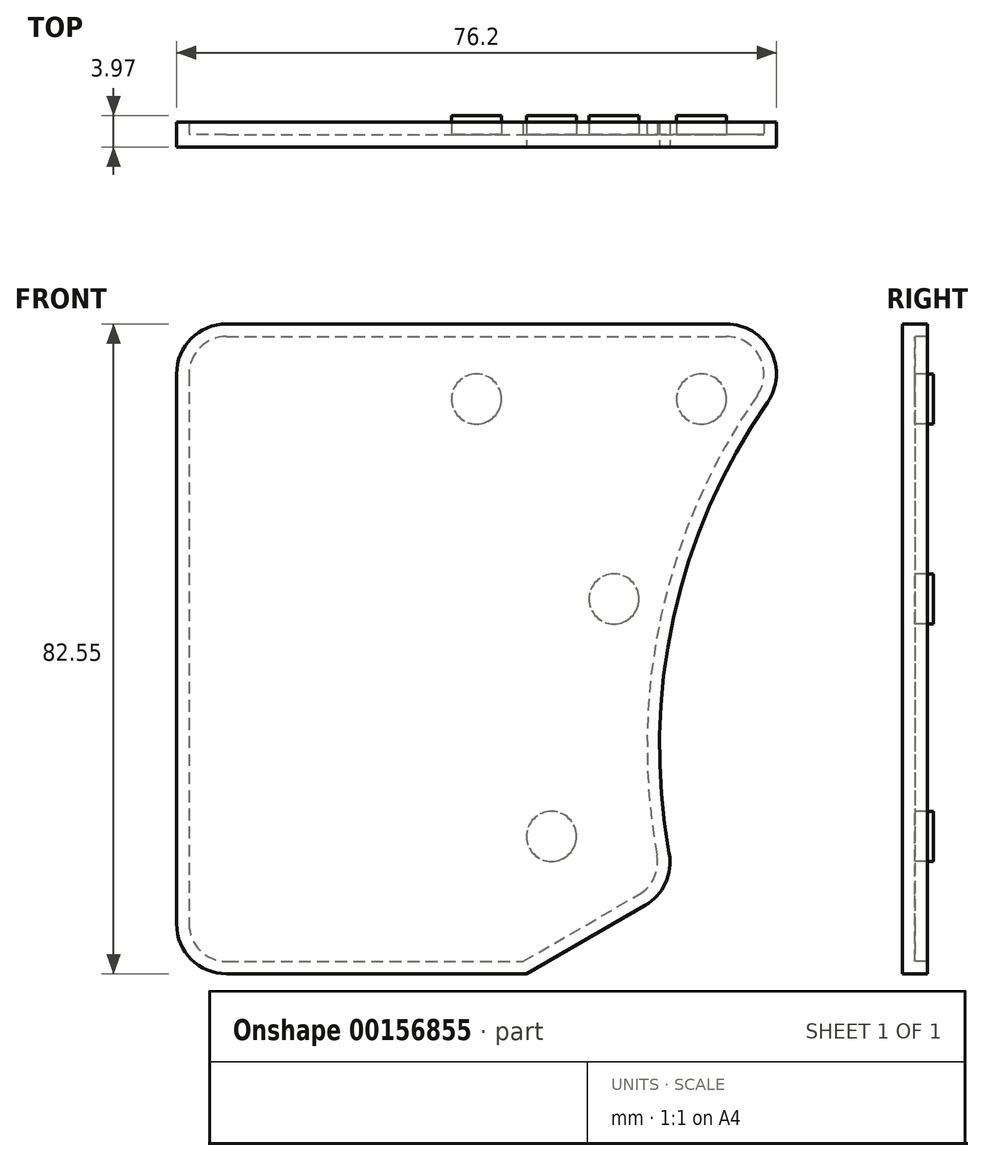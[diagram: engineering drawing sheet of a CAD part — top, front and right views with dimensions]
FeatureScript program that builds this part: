
annotation { "Feature Type Name" : "Feature", "Feature Type Description" : "" }
export const myFeature = defineFeature(function(context is Context, id is Id, definition is map)
    precondition{}
    {
        {
            var Q0;
            Q0=qCreatedBy(makeId("Front.planeOp"),FACE);
            var sketch = newSketch(context, id + "F0", { "sketchPlane" : qUnion([Q0])});
            skLineSegment(sketch, "E0", {"start": v(-19.05, 0) * mm, "end": v(44.45, 0) * mm});
            skLineSegment(sketch, "E1", {"start": v(-25.4, -6.35) * mm, "end": v(-25.4, -76.2) * mm});
            skLineSegment(sketch, "E2", {"start": v(-19.05, -82.55) * mm, "end": v(19.05, -82.55) * mm});
            skArc(sketch, "E3", {"start": v(49.66, -9.98) * mm, "mid": v(50.08, -3.41) * mm, "end": v(44.45, 0) * mm});
            skLineSegment(sketch, "E4", {"start": v(19.05, -82.55) * mm, "end": v(34.1, -73.86) * mm});
            skLineSegment(sketch, "E5", {"start": v(38.1, -71.55) * mm, "end": v(38.1, -82.55) * mm, "construction": true});
            skLineSegment(sketch, "E6", {"start": v(38.1, -82.55) * mm, "end": v(19.05, -82.55) * mm, "construction": true});
            skArc(sketch, "E7", {"start": v(49.66, -9.98) * mm, "mid": v(37.7, -37.35) * mm, "end": v(37.18, -67.22) * mm});
            skPoint(sketch, "E8.visualSharp", {"position": v(38.1, -71.55) * mm});
            skArc(sketch, "E8.filletArc", {"start": v(34.1, -73.86) * mm, "mid": v(36.7, -71.02) * mm, "end": v(37.18, -67.22) * mm});
            skPoint(sketch, "E9", {"position": v(50.8, -6.35) * mm});
            skPoint(sketch, "E10.visualSharp", {"position": v(-25.4, 0) * mm});
            skArc(sketch, "E10.filletArc", {"start": v(-19.05, 0) * mm, "mid": v(-23.54, -1.86) * mm, "end": v(-25.4, -6.35) * mm});
            skPoint(sketch, "E11.visualSharp", {"position": v(-25.4, -82.55) * mm});
            skArc(sketch, "E11.filletArc", {"start": v(-25.4, -76.2) * mm, "mid": v(-23.54, -80.7) * mm, "end": v(-19.05, -82.55) * mm});
            skSolve(sketch);
        }
        {
            var Q0;
            Q0=makeQuery(id+"F0.imprint","IMPRINT",FACE,{"disambiguationData":[TD([[makeQuery(id+"F0.imprint","IMPRINT",EDGE,{"derivedFrom":sQuery(id+"F0.wireOp",EDGE,"E0")}),-1.0]])]});
            extrude(context, id + "F1", {"entities" : qUnion([Q0]), "oppositeDirection" : true, "depth" : 3.17 * mm});
        }
        {
            var Q0;
            Q0=makeQuery(id+"F1.opExtrude","CAP_FACE",FACE,{"disambiguationData":[OSD([sQuery(id+"F0.wireOp",EDGE,"E0"),sQuery(id+"F0.wireOp",EDGE,"E1"),sQuery(id+"F0.wireOp",EDGE,"E2"),sQuery(id+"F0.wireOp",EDGE,"E3"),sQuery(id+"F0.wireOp",EDGE,"E4"),sQuery(id+"F0.wireOp",EDGE,"E7"),sQuery(id+"F0.wireOp",EDGE,"E8.filletArc"),sQuery(id+"F0.wireOp",EDGE,"E10.filletArc"),sQuery(id+"F0.wireOp",EDGE,"E11.filletArc")])],"isStart":false});
            shell(context, id + "F2", {"entities" : qUnion([Q0]), "thickness" : 1.59 * mm});
        }
        {
            var Q0;
            Q0=makeQuery(id+"F2.opShell","OFFSET_FACE",FACE,{"disambiguationData":[OSD([sQuery(id+"F0.wireOp",EDGE,"E0"),sQuery(id+"F0.wireOp",EDGE,"E1"),sQuery(id+"F0.wireOp",EDGE,"E2"),sQuery(id+"F0.wireOp",EDGE,"E3"),sQuery(id+"F0.wireOp",EDGE,"E4"),sQuery(id+"F0.wireOp",EDGE,"E7"),sQuery(id+"F0.wireOp",EDGE,"E8.filletArc"),sQuery(id+"F0.wireOp",EDGE,"E10.filletArc"),sQuery(id+"F0.wireOp",EDGE,"E11.filletArc")])]});
            var sketch = newSketch(context, id + "F3", { "sketchPlane" : qUnion([Q0])});
            skCircle(sketch, "E12", {"center": v(-41.28, -9.53) * mm, "radius": 3.18 * mm});
            skCircle(sketch, "E13", {"center": v(-12.7, -9.53) * mm, "radius": 3.18 * mm});
            skCircle(sketch, "E14", {"center": v(-30.16, -34.93) * mm, "radius": 3.18 * mm});
            skLineSegment(sketch, "E15", {"start": v(-12.7, -9.53) * mm, "end": v(-41.28, -9.53) * mm, "construction": true});
            skCircle(sketch, "E16", {"center": v(-22.23, -65.09) * mm, "radius": 3.18 * mm});
            skSolve(sketch);
        }
        {
            var Q0;
            Q0=makeQuery(id+"F3.imprint","IMPRINT",FACE,{"disambiguationData":[TD([[makeQuery(id+"F3.imprint","IMPRINT",EDGE,{"derivedFrom":sQuery(id+"F3.wireOp",EDGE,"E12")}),1.0]])]});
            var Q1;
            Q1=makeQuery(id+"F3.imprint","IMPRINT",FACE,{"disambiguationData":[TD([[makeQuery(id+"F3.imprint","IMPRINT",EDGE,{"derivedFrom":sQuery(id+"F3.wireOp",EDGE,"E13")}),1.0]])]});
            var Q2;
            Q2=makeQuery(id+"F3.imprint","IMPRINT",FACE,{"disambiguationData":[TD([[makeQuery(id+"F3.imprint","IMPRINT",EDGE,{"derivedFrom":sQuery(id+"F3.wireOp",EDGE,"E14")}),1.0]])]});
            var Q3;
            Q3=makeQuery(id+"F3.imprint","IMPRINT",FACE,{"disambiguationData":[TD([[makeQuery(id+"F3.imprint","IMPRINT",EDGE,{"derivedFrom":sQuery(id+"F3.wireOp",EDGE,"E16")}),1.0]])]});
            extrude(context, id + "F4", {"entities" : qUnion([Q0, Q1, Q2, Q3]), "operationType" : NewBodyOperationType.ADD, "depth" : 2.38 * mm});
        }
    });
